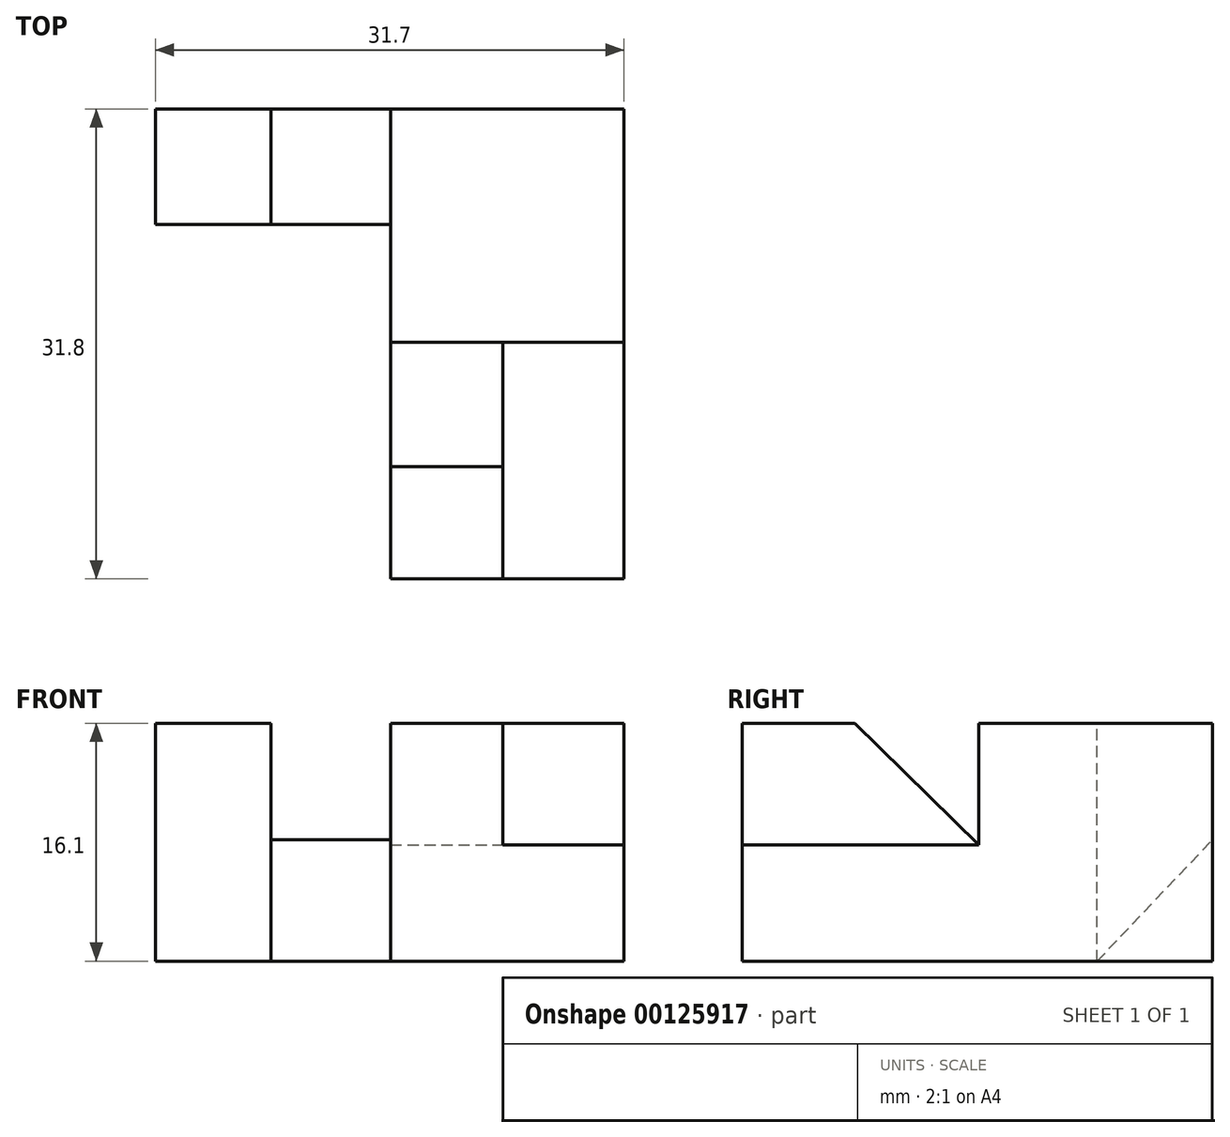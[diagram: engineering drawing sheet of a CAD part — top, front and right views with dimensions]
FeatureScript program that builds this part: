
annotation { "Feature Type Name" : "Feature", "Feature Type Description" : "" }
export const myFeature = defineFeature(function(context is Context, id is Id, definition is map)
    precondition{}
    {
        {
            var Q0;
            Q0=qCreatedBy(makeId("Top.planeOp"),FACE);
            var sketch = newSketch(context, id + "F0", { "sketchPlane" : qUnion([Q0])});
            skLineSegment(sketch, "E0.bottom", {"start": v(-8.6, -9.09) * mm, "end": v(7.2, -9.09) * mm});
            skLineSegment(sketch, "E0.top", {"start": v(-8.6, 6.71) * mm, "end": v(7.2, 6.71) * mm});
            skLineSegment(sketch, "E0.left", {"start": v(-8.6, -9.09) * mm, "end": v(-8.6, 6.71) * mm});
            skLineSegment(sketch, "E0.right", {"start": v(7.2, -9.09) * mm, "end": v(7.2, 6.71) * mm});
            skSolve(sketch);
        }
        {
            var Q0;
            Q0=makeQuery(id+"F0.imprint","IMPRINT",FACE,{"disambiguationData":[TD([[makeQuery(id+"F0.imprint","IMPRINT",EDGE,{"derivedFrom":sQuery(id+"F0.wireOp",EDGE,"E0.bottom")}),1.0]])]});
            extrude(context, id + "F1", {"entities" : qUnion([Q0]), "depth" : 16.1 * mm});
        }
        {
            var Q0;
            Q0=makeQuery(id+"F1.opExtrude","SWEPT_FACE",FACE,{"disambiguationData":[OSD([sQuery(id+"F0.wireOp",EDGE,"E0.left")])]});
            var sketch = newSketch(context, id + "F2", { "sketchPlane" : qUnion([Q0])});
            skLineSegment(sketch, "E1", {"start": v(9.09, 0) * mm, "end": v(9.09, 8.2) * mm});
            skLineSegment(sketch, "E2", {"start": v(9.09, 0) * mm, "end": v(1.29, 0) * mm});
            skLineSegment(sketch, "E3", {"start": v(1.29, 0) * mm, "end": v(9.09, 8.2) * mm});
            skSolve(sketch);
        }
        {
            var Q0;
            Q0=makeQuery(id+"F2.imprint","IMPRINT",FACE,{"disambiguationData":[TD([[makeQuery(id+"F2.imprint","IMPRINT",EDGE,{"derivedFrom":sQuery(id+"F2.wireOp",EDGE,"E1")}),-1.0]])]});
            extrude(context, id + "F3", {"entities" : qUnion([Q0]), "operationType" : NewBodyOperationType.ADD, "depth" : 8.1 * mm});
        }
        {
            var Q0;
            Q0=makeQuery(id+"F3.opExtrude","CAP_FACE",FACE,{"disambiguationData":[OSD([sQuery(id+"F2.wireOp",EDGE,"E1"),sQuery(id+"F2.wireOp",EDGE,"E2"),sQuery(id+"F2.wireOp",EDGE,"E3")])],"isStart":false});
            var sketch = newSketch(context, id + "F4", { "sketchPlane" : qUnion([Q0])});
            skLineSegment(sketch, "E4.bottom", {"start": v(9.09, 0) * mm, "end": v(1.29, 0) * mm});
            skLineSegment(sketch, "E4.top", {"start": v(9.09, 16.1) * mm, "end": v(1.29, 16.1) * mm});
            skLineSegment(sketch, "E4.left", {"start": v(9.09, 0) * mm, "end": v(9.09, 16.1) * mm});
            skLineSegment(sketch, "E4.right", {"start": v(1.29, 0) * mm, "end": v(1.29, 16.1) * mm});
            skSolve(sketch);
        }
        {
            var Q0;
            {var subQ0=sQuery(id+"F4.wireOp",EDGE,"E4.top");Q0=makeQuery(id+"F4.imprint","IMPRINT",FACE,{"disambiguationData":[TD([[makeQuery(id+"F4.imprint","IMPRINT",EDGE,{"derivedFrom":subQ0}),1.0]])]});}
            var Q1;
            {var subQ0=sQuery(id+"F4.wireOp",EDGE,"E4.bottom");Q1=makeQuery(id+"F4.imprint","IMPRINT",FACE,{"disambiguationData":[TD([[makeQuery(id+"F4.imprint","IMPRINT",EDGE,{"derivedFrom":subQ0}),-1.0]])]});}
            extrude(context, id + "F5", {"entities" : qUnion([Q0, Q1]), "operationType" : NewBodyOperationType.ADD, "depth" : 7.8 * mm});
        }
        {
            var Q0;
            Q0=makeQuery(id+"F5.boolean.opBoolean","MERGE",FACE,{"derivedFrom":[makeQuery(id+"F3.boolean.opBoolean","MERGE",FACE,{"derivedFrom":[makeQuery(id+"F1.opExtrude","CAP_FACE",FACE,{"disambiguationData":[OSD([sQuery(id+"F0.wireOp",EDGE,"E0.bottom"),sQuery(id+"F0.wireOp",EDGE,"E0.top"),sQuery(id+"F0.wireOp",EDGE,"E0.left"),sQuery(id+"F0.wireOp",EDGE,"E0.right")])],"isStart":true}),makeQuery(id+"F3.opExtrude","SWEPT_FACE",FACE,{"disambiguationData":[OSD([sQuery(id+"F2.wireOp",EDGE,"E2")])]})]}),makeQuery(id+"F5.opExtrude","SWEPT_FACE",FACE,{"disambiguationData":[OSD([sQuery(id+"F4.wireOp",EDGE,"E4.bottom")])]})]});
            var sketch = newSketch(context, id + "F6", { "sketchPlane" : qUnion([Q0])});
            skLineSegment(sketch, "E5.bottom", {"start": v(7.2, -6.71) * mm, "end": v(-8.6, -6.71) * mm});
            skLineSegment(sketch, "E5.top", {"start": v(7.2, -22.71) * mm, "end": v(-8.6, -22.71) * mm});
            skLineSegment(sketch, "E5.left", {"start": v(7.2, -6.71) * mm, "end": v(7.2, -22.71) * mm});
            skLineSegment(sketch, "E5.right", {"start": v(-8.6, -6.71) * mm, "end": v(-8.6, -22.71) * mm});
            skSolve(sketch);
        }
        {
            var Q0;
            Q0=makeQuery(id+"F6.imprint","IMPRINT",FACE,{"disambiguationData":[TD([[makeQuery(id+"F6.imprint","IMPRINT",EDGE,{"derivedFrom":sQuery(id+"F6.wireOp",EDGE,"E5.bottom")}),-1.0]])]});
            extrude(context, id + "F7", {"entities" : qUnion([Q0]), "operationType" : NewBodyOperationType.ADD, "oppositeDirection" : true, "depth" : 7.85 * mm});
        }
        {
            var Q0;
            Q0=makeQuery(id+"F7.opExtrude","CAP_FACE",FACE,{"disambiguationData":[OSD([sQuery(id+"F6.wireOp",EDGE,"E5.bottom"),sQuery(id+"F6.wireOp",EDGE,"E5.top"),sQuery(id+"F6.wireOp",EDGE,"E5.left"),sQuery(id+"F6.wireOp",EDGE,"E5.right")])],"isStart":false});
            var sketch = newSketch(context, id + "F8", { "sketchPlane" : qUnion([Q0])});
            skLineSegment(sketch, "E6.bottom", {"start": v(-8.6, 22.71) * mm, "end": v(-1, 22.71) * mm});
            skLineSegment(sketch, "E6.top", {"start": v(-8.6, 15.11) * mm, "end": v(-1, 15.11) * mm});
            skLineSegment(sketch, "E6.left", {"start": v(-8.6, 22.71) * mm, "end": v(-8.6, 15.11) * mm});
            skLineSegment(sketch, "E6.right", {"start": v(-1, 22.71) * mm, "end": v(-1, 15.11) * mm});
            skSolve(sketch);
        }
        {
            var Q0;
            Q0=makeQuery(id+"F8.imprint","IMPRINT",FACE,{"disambiguationData":[TD([[makeQuery(id+"F8.imprint","IMPRINT",EDGE,{"derivedFrom":sQuery(id+"F8.wireOp",EDGE,"E6.bottom")}),1.0]])]});
            var Q1;
            Q1=makeQuery(id+"F1.opExtrude","CAP_FACE",FACE,{"disambiguationData":[OSD([sQuery(id+"F0.wireOp",EDGE,"E0.bottom"),sQuery(id+"F0.wireOp",EDGE,"E0.top"),sQuery(id+"F0.wireOp",EDGE,"E0.left"),sQuery(id+"F0.wireOp",EDGE,"E0.right")])],"isStart":false});
            extrude(context, id + "F9", {"entities" : qUnion([Q0]), "operationType" : NewBodyOperationType.ADD, "endBound" : BoundingType.UP_TO_SURFACE, "endBoundEntityFace" : qUnion([Q1]), "depth" : 25.4 * mm});
        }
        {
            var Q0;
            Q0=makeQuery(id+"F9.boolean.opBoolean","MERGE",FACE,{"derivedFrom":[makeQuery(id+"F7.opExtrude","SWEPT_FACE",FACE,{"disambiguationData":[OSD([sQuery(id+"F6.wireOp",EDGE,"E5.right")])]}),makeQuery(id+"F9.opExtrude","SWEPT_FACE",FACE,{"disambiguationData":[OSD([sQuery(id+"F8.wireOp",EDGE,"E6.left")])]})]});
            var sketch = newSketch(context, id + "F10", { "sketchPlane" : qUnion([Q0])});
            skLineSegment(sketch, "E7", {"start": v(-15.11, 16.1) * mm, "end": v(-6.71, 7.85) * mm});
            skSolve(sketch);
        }
        {
            var Q0;
            Q0=makeQuery(id+"F10.imprint","IMPRINT",FACE,{"disambiguationData":[TD([[makeQuery(id+"F10.imprint","IMPRINT",EDGE,{"derivedFrom":sQuery(id+"F10.wireOp",EDGE,"E7")}),-1.0]])]});
            var Q1;
            Q1=makeQuery(id+"F9.opExtrude","SWEPT_FACE",FACE,{"disambiguationData":[OSD([sQuery(id+"F8.wireOp",EDGE,"E6.right")])]});
            extrude(context, id + "F11", {"entities" : qUnion([Q0]), "operationType" : NewBodyOperationType.ADD, "endBound" : BoundingType.UP_TO_SURFACE, "oppositeDirection" : true, "endBoundEntityFace" : qUnion([Q1]), "depth" : 25.4 * mm});
        }
        {
            var Q0;
            Q0=makeQuery(id+"F1.opExtrude","SWEPT_BODY",BODY,{"disambiguationData":[OSD([sQuery(id+"F0.wireOp",EDGE,"E0.bottom"),sQuery(id+"F0.wireOp",EDGE,"E0.top"),sQuery(id+"F0.wireOp",EDGE,"E0.left"),sQuery(id+"F0.wireOp",EDGE,"E0.right")])]});
            var Q1;
            Q1=makeQuery(id+"F5.boolean.opBoolean","MERGE",FACE,{"derivedFrom":[makeQuery(id+"F3.boolean.opBoolean","MERGE",FACE,{"derivedFrom":[makeQuery(id+"F1.opExtrude","SWEPT_FACE",FACE,{"disambiguationData":[OSD([sQuery(id+"F0.wireOp",EDGE,"E0.bottom")])]}),makeQuery(id+"F3.opExtrude","SWEPT_FACE",FACE,{"disambiguationData":[OSD([sQuery(id+"F2.wireOp",EDGE,"E1")])]})]}),makeQuery(id+"F5.opExtrude","SWEPT_FACE",FACE,{"disambiguationData":[OSD([sQuery(id+"F4.wireOp",EDGE,"E4.left")])]})]});
            mirror(context, id + "F12", {"operationType" : NewBodyOperationType.ADD, "entities" : qUnion([Q0]), "mirrorPlane" : qUnion([Q1])});
        }
        {
            var Q0;
            {var subQ0=makeQuery(id+"F5.opExtrude","SWEPT_FACE",FACE,{"disambiguationData":[OSD([sQuery(id+"F4.wireOp",EDGE,"E4.top")])]});Q0=makeQuery(id+"F12.boolean.opBoolean","MERGE",FACE,{"derivedFrom":[subQ0,makeQuery(id+"F12.opPattern","COPY",FACE,{"derivedFrom":subQ0,"instanceName":"1"})]});}
            var sketch = newSketch(context, id + "F13", { "sketchPlane" : qUnion([Q0])});
            skPoint(sketch, "E8.start.orphan", {"position": v(-24.5, -9.09) * mm});
            skLineSegment(sketch, "E9", {"start": v(-24.5, -9.09) * mm, "end": v(7.2, -9.09) * mm});
            skPoint(sketch, "E10.orphan", {"position": v(7.2, -24.89) * mm});
            skPoint(sketch, "E11.0.end.orphan", {"position": v(7.2, 6.71) * mm});
            skLineSegment(sketch, "E12", {"start": v(7.2, -9.09) * mm, "end": v(7.2, 22.71) * mm});
            skPoint(sketch, "E13.0.end.orphan", {"position": v(-1, 22.71) * mm});
            skLineSegment(sketch, "E14", {"start": v(7.2, 22.71) * mm, "end": v(-24.5, 22.71) * mm});
            skLineSegment(sketch, "E15", {"start": v(-24.5, -9.09) * mm, "end": v(-24.5, 22.71) * mm});
            skSolve(sketch);
        }
        {
            var Q0;
            {var subQ4=sQuery(id+"F13.wireOp",EDGE,"E12");Q0=makeQuery(id+"F13.imprint","IMPRINT",FACE,{"disambiguationData":[TD([[makeQuery(id+"F13.imprint","IMPRINT",EDGE,{"derivedFrom":subQ4}),1.0]])]});}
            var Q1;
            {var subQ2=sQuery(id+"F4.wireOp",EDGE,"E4.top");var subQ8=makeQuery(id+"F5.opExtrude","SWEPT_EDGE",EDGE,{"disambiguationData":[OSD([subQ2,sQuery(id+"F4.wireOp",EDGE,"E4.right")])]});Q1=makeQuery(id+"F13.imprint","IMPRINT",FACE,{"disambiguationData":[TD([[makeQuery(id+"F13.imprint","IMPRINT",EDGE,{"derivedFrom":subQ8}),-1.0]])]});}
            extrude(context, id + "F14", {"entities" : qUnion([Q0, Q1]), "operationType" : NewBodyOperationType.REMOVE, "oppositeDirection" : true, "depth" : 25.4 * mm, "offsetDistance" : 25.4 * mm});
        }
    });
